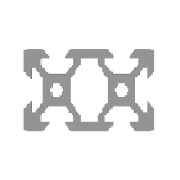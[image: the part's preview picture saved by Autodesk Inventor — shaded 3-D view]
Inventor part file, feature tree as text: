
AUTODESK INVENTOR PART (.ipt)
format: ipt  version: 2013 (Build 170138000, 138)  size: 217,088 bytes
history: native  units: mm
features: other x4, plane x3, split x2, sketch x2
ambient origin geometry x8: Origin, YZ Plane, XZ Plane, XY Plane, X Axis, Y Axis, Z Axis, Center Point
bodies: Solid1 (feature_tree), Body (feature_tree)
feature tree (11):
  other  "Driven Length"
  other  "Frame Generator"
  other  "Start Plane"
  other  "End Plane"
  plane  "Work Plane6"
  split  "Split1"
  plane  "Work Plane7"
  split  "Split2"
  sketch  "Sketch8"  dims[d2=10.0mm]
  plane  "Work Plane5"
  sketch  "Sketch9"  dims[d26=10.0mm d27=10.0mm d28=4.2mm d29=1.5mm d30=45.0deg d32=45.0deg d33=1.64mm d34=1.8mm d35=10.0mm d36=5.68mm d37=30.0mm d39=180.0deg d41=1.96mm d42=5.68mm d45=1.8mm d46=10.0mm d47=340.0mm d48=0.13mm d49=0.0mm d54=90.0deg d51=330.0mm]
